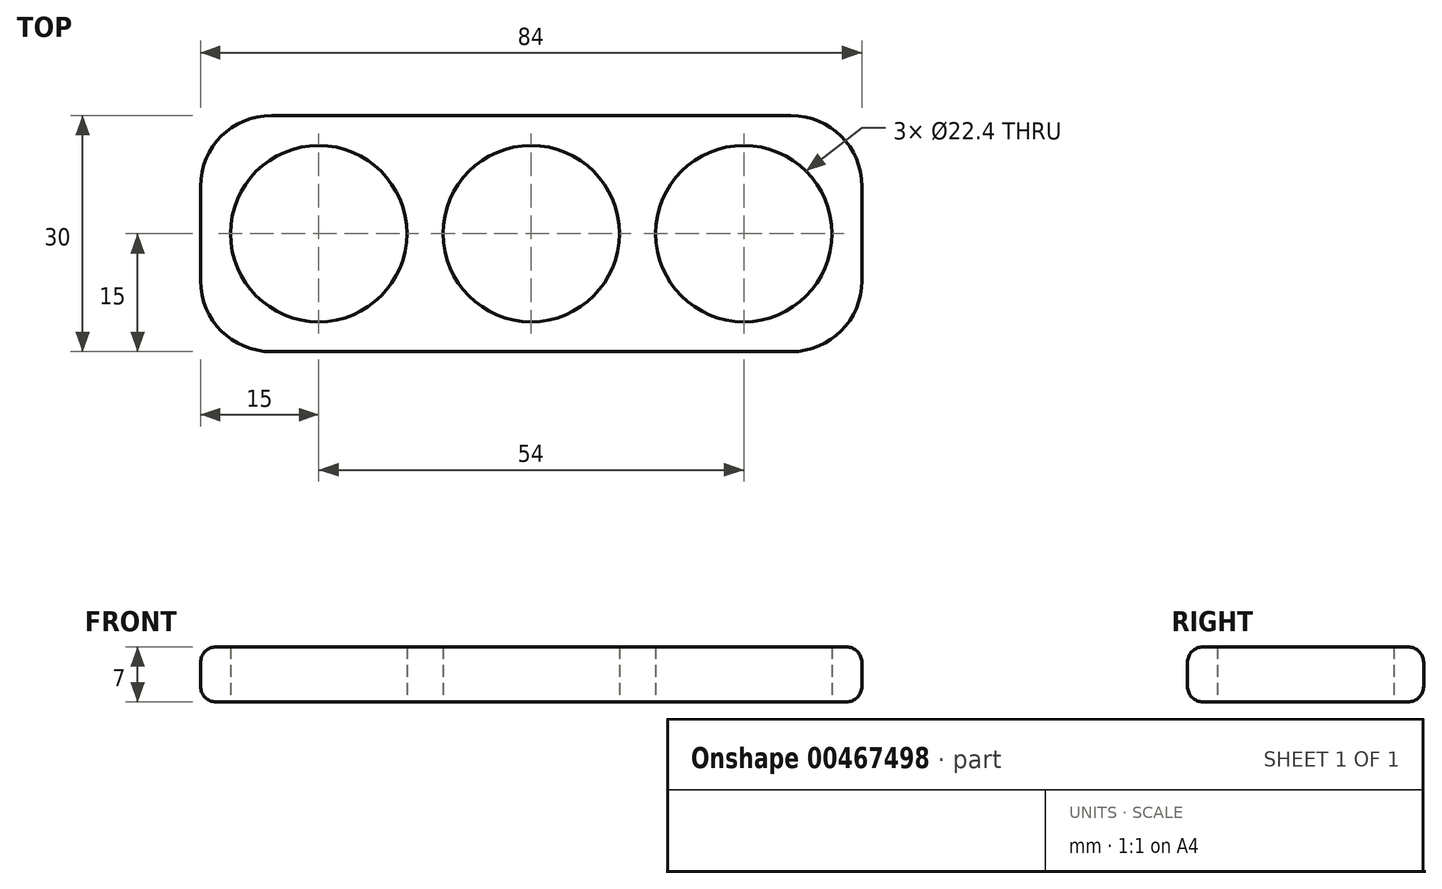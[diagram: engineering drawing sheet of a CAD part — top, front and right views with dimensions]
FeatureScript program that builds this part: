
annotation { "Feature Type Name" : "Feature", "Feature Type Description" : "" }
export const myFeature = defineFeature(function(context is Context, id is Id, definition is map)
    precondition{}
    {
        {
            var Q0;
            Q0=qCreatedBy(makeId("Top.planeOp"),FACE);
            var sketch = newSketch(context, id + "F0", { "sketchPlane" : qUnion([Q0])});
            skCircle(sketch, "E0", {"center": v(0, 0) * mm, "radius": 11.2 * mm});
            skCircle(sketch, "E1", {"center": v(27, 0) * mm, "radius": 11.2 * mm});
            skCircle(sketch, "E2", {"center": v(-27, 0) * mm, "radius": 11.2 * mm});
            skLineSegment(sketch, "E3", {"start": v(0, 15) * mm, "end": v(42, 15) * mm});
            skLineSegment(sketch, "E4", {"start": v(42, 15) * mm, "end": v(42, -15) * mm});
            skLineSegment(sketch, "E5", {"start": v(42, -15) * mm, "end": v(-42, -15) * mm});
            skLineSegment(sketch, "E6", {"start": v(-42, -15) * mm, "end": v(-42, 15) * mm});
            skLineSegment(sketch, "E7", {"start": v(-42, 15) * mm, "end": v(0, 15) * mm});
            skSolve(sketch);
        }
        {
            var Q0;
            Q0=makeQuery(id+"F0.imprint","IMPRINT",FACE,{"disambiguationData":[TD([[makeQuery(id+"F0.imprint","IMPRINT",EDGE,{"derivedFrom":sQuery(id+"F0.wireOp",EDGE,"E0")}),-1.0]])]});
            extrude(context, id + "F1", {"entities" : qUnion([Q0]), "depth" : 7 * mm});
        }
        {
            var Q0;
            Q0=makeQuery(id+"F1.opExtrude","CAP_EDGE",EDGE,{"disambiguationData":[OSD([sQuery(id+"F0.wireOp",EDGE,"E3"),sQuery(id+"F0.wireOp",EDGE,"E7")])],"isStart":false});
            var Q1;
            Q1=makeQuery(id+"F1.opExtrude","CAP_EDGE",EDGE,{"disambiguationData":[OSD([sQuery(id+"F0.wireOp",EDGE,"E6")])],"isStart":false});
            var Q2;
            Q2=makeQuery(id+"F1.opExtrude","CAP_EDGE",EDGE,{"disambiguationData":[OSD([sQuery(id+"F0.wireOp",EDGE,"E5")])],"isStart":false});
            var Q3;
            Q3=makeQuery(id+"F1.opExtrude","CAP_EDGE",EDGE,{"disambiguationData":[OSD([sQuery(id+"F0.wireOp",EDGE,"E4")])],"isStart":false});
            var Q4;
            Q4=makeQuery(id+"F1.opExtrude","CAP_EDGE",EDGE,{"disambiguationData":[OSD([sQuery(id+"F0.wireOp",EDGE,"E4")])],"isStart":true});
            var Q5;
            Q5=makeQuery(id+"F1.opExtrude","CAP_EDGE",EDGE,{"disambiguationData":[OSD([sQuery(id+"F0.wireOp",EDGE,"E3"),sQuery(id+"F0.wireOp",EDGE,"E7")])],"isStart":true});
            var Q6;
            Q6=makeQuery(id+"F1.opExtrude","CAP_EDGE",EDGE,{"disambiguationData":[OSD([sQuery(id+"F0.wireOp",EDGE,"E6")])],"isStart":true});
            var Q7;
            Q7=makeQuery(id+"F1.opExtrude","CAP_EDGE",EDGE,{"disambiguationData":[OSD([sQuery(id+"F0.wireOp",EDGE,"E5")])],"isStart":true});
            fillet(context, id + "F2", {"entities" : qUnion([Q0, Q1, Q2, Q3, Q4, Q5, Q6, Q7]), "radius" : 2 * mm, "tangentPropagation" : true, "allowEdgeOverflow" : false});
        }
        {
            var Q0;
            Q0=makeQuery(id+"F1.opExtrude","SWEPT_EDGE",EDGE,{"disambiguationData":[OSD([sQuery(id+"F0.wireOp",EDGE,"E6"),sQuery(id+"F0.wireOp",EDGE,"E7")])]});
            var Q1;
            Q1=makeQuery(id+"F1.opExtrude","SWEPT_EDGE",EDGE,{"disambiguationData":[OSD([sQuery(id+"F0.wireOp",EDGE,"E5"),sQuery(id+"F0.wireOp",EDGE,"E6")])]});
            var Q2;
            Q2=makeQuery(id+"F1.opExtrude","SWEPT_EDGE",EDGE,{"disambiguationData":[OSD([sQuery(id+"F0.wireOp",EDGE,"E4"),sQuery(id+"F0.wireOp",EDGE,"E5")])]});
            var Q3;
            Q3=makeQuery(id+"F1.opExtrude","SWEPT_EDGE",EDGE,{"disambiguationData":[OSD([sQuery(id+"F0.wireOp",EDGE,"E3"),sQuery(id+"F0.wireOp",EDGE,"E4")])]});
            fillet(context, id + "F3", {"entities" : qUnion([Q0, Q1, Q2, Q3]), "radius" : 9 * mm, "tangentPropagation" : true, "allowEdgeOverflow" : false});
        }
    });
